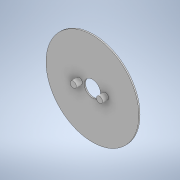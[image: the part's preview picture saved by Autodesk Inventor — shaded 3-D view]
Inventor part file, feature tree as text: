
AUTODESK INVENTOR PART (.ipt)
format: ipt  version: 2022 (Build 260153000, 153)  size: 108,032 bytes
history: native  units: mm
features: extrude x2, sketch x2, other x1
ambient origin geometry x8: Origin, YZ Plane, XZ Plane, XY Plane, X Axis, Y Axis, Z Axis, Center Point
bodies: Body1 (feature_tree)
feature tree (5):
  other  "ソリッド1"
  extrude  "押し出し1"  Depth=46.0mm
  extrude  "押し出し2"  Depth=8.0mm
  sketch  "スケッチ1"
  sketch  "スケッチ2"
